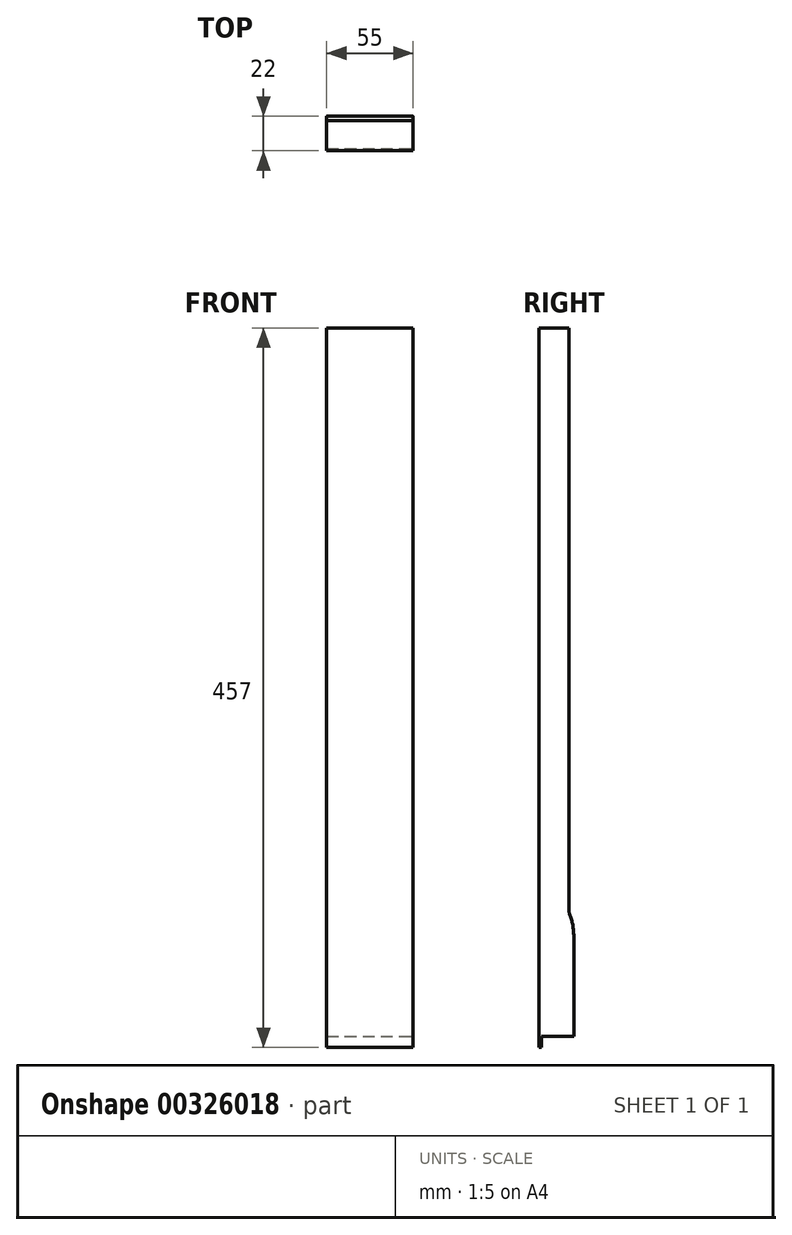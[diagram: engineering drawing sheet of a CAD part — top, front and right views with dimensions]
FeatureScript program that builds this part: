
annotation { "Feature Type Name" : "Feature", "Feature Type Description" : "" }
export const myFeature = defineFeature(function(context is Context, id is Id, definition is map)
    precondition{}
    {
        {
            var Q0;
            Q0=qCreatedBy(makeId("Front.planeOp"),FACE);
            var sketch = newSketch(context, id + "F0", { "sketchPlane" : qUnion([Q0])});
            skLineSegment(sketch, "E0.bottom", {"start": v(-27.5, 225) * mm, "end": v(27.5, 225) * mm});
            skLineSegment(sketch, "E0.top", {"start": v(-27.5, -225) * mm, "end": v(27.5, -225) * mm});
            skLineSegment(sketch, "E0.left", {"start": v(-27.5, 225) * mm, "end": v(-27.5, -225) * mm});
            skLineSegment(sketch, "E0.right", {"start": v(27.5, 225) * mm, "end": v(27.5, -225) * mm});
            skPoint(sketch, "E0.middle", {"position": v(0, 0) * mm});
            skSolve(sketch);
        }
        {
            var Q0;
            Q0 = qSketchRegion(id + "F0", true);
            extrude(context, id + "F1", {"entities" : qUnion([Q0]), "depth" : 22 * mm});
        }
        {
            var Q0;
            Q0=makeQuery(id+"F1.opExtrude","SWEPT_FACE",FACE,{"disambiguationData":[OSD([sQuery(id+"F0.wireOp",EDGE,"E0.top")])]});
            var sketch = newSketch(context, id + "F2", { "sketchPlane" : qUnion([Q0])});
            skLineSegment(sketch, "E1.bottom", {"start": v(-27.5, 20.5) * mm, "end": v(27.5, 20.5) * mm});
            skLineSegment(sketch, "E1.top", {"start": v(-27.5, 22) * mm, "end": v(27.5, 22) * mm});
            skLineSegment(sketch, "E1.left", {"start": v(-27.5, 20.5) * mm, "end": v(-27.5, 22) * mm});
            skLineSegment(sketch, "E1.right", {"start": v(27.5, 20.5) * mm, "end": v(27.5, 22) * mm});
            skSolve(sketch);
        }
        {
            var Q0;
            Q0 = qSketchRegion(id + "F2", true);
            extrude(context, id + "F3", {"entities" : qUnion([Q0]), "operationType" : NewBodyOperationType.ADD, "depth" : 7 * mm});
        }
        {
            var Q0;
            Q0=makeQuery(id+"F3.boolean.opBoolean","MERGE",FACE,{"derivedFrom":[makeQuery(id+"F1.opExtrude","SWEPT_FACE",FACE,{"disambiguationData":[OSD([sQuery(id+"F0.wireOp",EDGE,"E0.left")])]}),makeQuery(id+"F3.opExtrude","SWEPT_FACE",FACE,{"disambiguationData":[OSD([sQuery(id+"F2.wireOp",EDGE,"E1.left")])]})]});
            var sketch = newSketch(context, id + "F4", { "sketchPlane" : qUnion([Q0])});
            skLineSegment(sketch, "E2.bottom", {"start": v(0, -150) * mm, "end": v(3, -150) * mm});
            skLineSegment(sketch, "E2.top", {"start": v(0, 225) * mm, "end": v(3, 225) * mm});
            skLineSegment(sketch, "E2.left", {"start": v(0, -150) * mm, "end": v(0, 225) * mm});
            skLineSegment(sketch, "E2.right", {"start": v(3, -150) * mm, "end": v(3, 225) * mm});
            skSolve(sketch);
        }
        {
            var Q0;
            Q0 = qSketchRegion(id + "F4", true);
            extrude(context, id + "F5", {"entities" : qUnion([Q0]), "operationType" : NewBodyOperationType.REMOVE, "endBound" : BoundingType.THROUGH_ALL, "oppositeDirection" : true, "depth" : 25 * mm});
        }
        {
            var Q0;
            Q0=makeQuery(id+"F5.boolean.opBoolean","COPY",EDGE,{"derivedFrom":makeQuery(id+"F5.opExtrude","SWEPT_EDGE",EDGE,{"disambiguationData":[OSD([sQuery(id+"F4.wireOp",EDGE,"E2.bottom"),sQuery(id+"F4.wireOp",EDGE,"E2.right")])]})});
            fillet(context, id + "F6", {"entities" : qUnion([Q0]), "radius" : 5 * mm, "tangentPropagation" : true, "allowEdgeOverflow" : false});
        }
        {
            var Q0;
            Q0=makeQuery(id+"F6.opFillet","BLEND_EDGE",EDGE,{"blendedFrom":[makeQuery(id+"F5.boolean.opBoolean","COPY",EDGE,{"derivedFrom":makeQuery(id+"F5.opExtrude","SWEPT_EDGE",EDGE,{"disambiguationData":[OSD([sQuery(id+"F4.wireOp",EDGE,"E2.bottom"),sQuery(id+"F4.wireOp",EDGE,"E2.right")])]})}),makeQuery(id+"F1.opExtrude","CAP_FACE",FACE,{"disambiguationData":[OSD([sQuery(id+"F0.wireOp",EDGE,"E0.bottom"),sQuery(id+"F0.wireOp",EDGE,"E0.top"),sQuery(id+"F0.wireOp",EDGE,"E0.left"),sQuery(id+"F0.wireOp",EDGE,"E0.right")])],"isStart":true})],"blendedInto":[makeQuery(id+"F1.opExtrude","CAP_FACE",FACE,{"disambiguationData":[OSD([sQuery(id+"F0.wireOp",EDGE,"E0.bottom"),sQuery(id+"F0.wireOp",EDGE,"E0.top"),sQuery(id+"F0.wireOp",EDGE,"E0.left"),sQuery(id+"F0.wireOp",EDGE,"E0.right")])],"isStart":true})]});
            fillet(context, id + "F7", {"entities" : qUnion([Q0]), "radius" : 40 * mm, "tangentPropagation" : true, "allowEdgeOverflow" : false});
        }
    });
